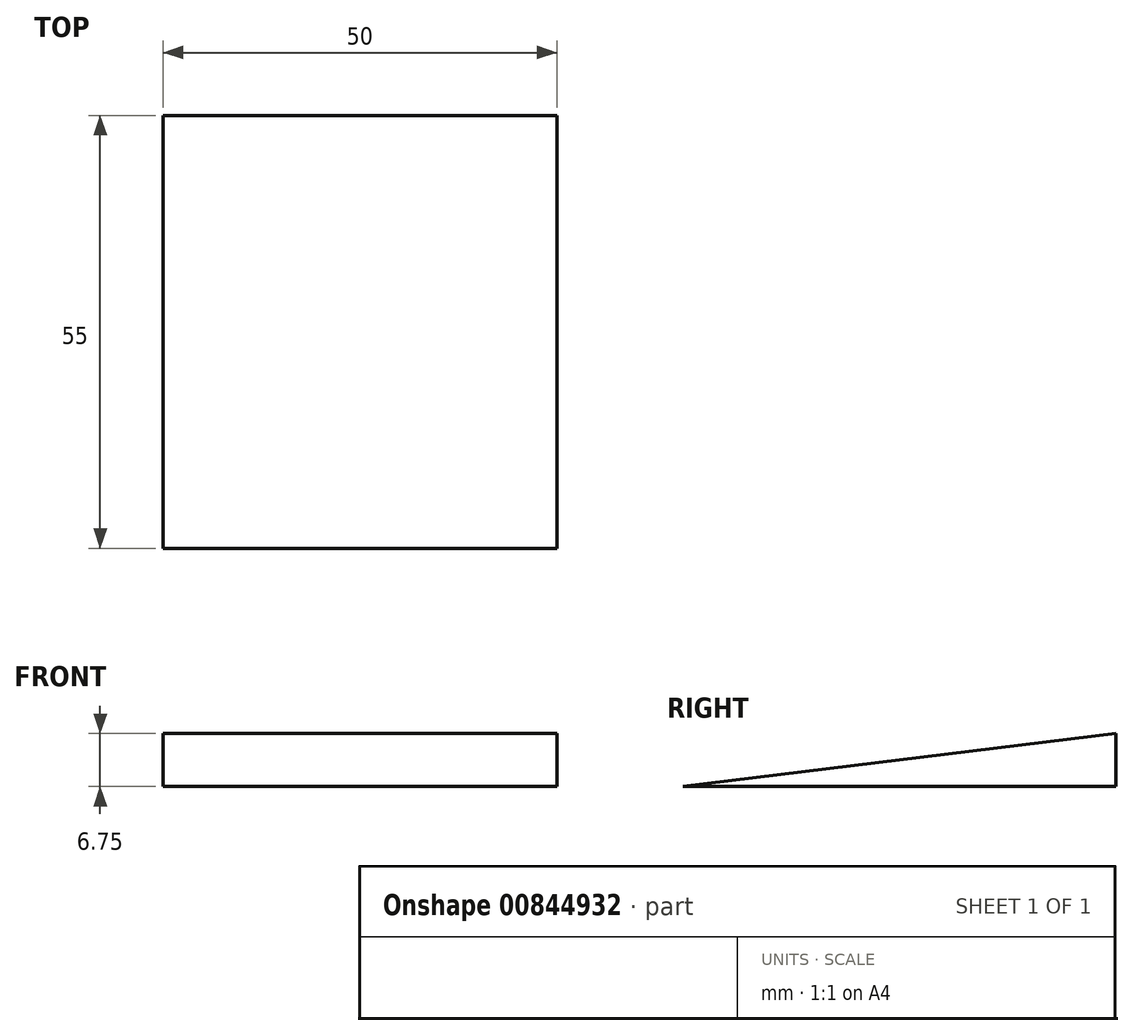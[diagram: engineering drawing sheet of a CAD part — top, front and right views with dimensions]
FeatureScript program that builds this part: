
annotation { "Feature Type Name" : "Feature", "Feature Type Description" : "" }
export const myFeature = defineFeature(function(context is Context, id is Id, definition is map)
    precondition{}
    {
        {
            var Q0;
            Q0=qCreatedBy(makeId("Top.planeOp"),FACE);
            var sketch = newSketch(context, id + "F0", { "sketchPlane" : qUnion([Q0])});
            skLineSegment(sketch, "E0.bottom", {"start": v(25, 27.5) * mm, "end": v(-25, 27.5) * mm});
            skLineSegment(sketch, "E0.top", {"start": v(25, -27.5) * mm, "end": v(-25, -27.5) * mm});
            skLineSegment(sketch, "E0.left", {"start": v(25, 27.5) * mm, "end": v(25, -27.5) * mm});
            skLineSegment(sketch, "E0.right", {"start": v(-25, 27.5) * mm, "end": v(-25, -27.5) * mm});
            skPoint(sketch, "E0.middle", {"position": v(0, 0) * mm});
            skSolve(sketch);
        }
        {
            var Q0;
            Q0=qCreatedBy(makeId("Top.planeOp"),FACE);
            var sketch = newSketch(context, id + "F1", { "sketchPlane" : qUnion([Q0])});
            skLineSegment(sketch, "E1", {"start": v(-25, -27.5) * mm, "end": v(25, -27.5) * mm});
            skSolve(sketch);
        }
        {
            var Q0;
            Q0 = qBodyType(qCreatedBy(id + "F1" ,EDGE), BodyType.WIRE);
            cPlane(context, id + "F2", {"entities" : qUnion([Q0]), "cplaneType" : CPlaneType.LINE_ANGLE, "offset" : 25 * mm, "angle" : 97 * degree, "width" : 150 * mm, "height" : 150 * mm});
        }
        {
            var Q0;
            Q0=makeQuery(id+"F0.imprint","IMPRINT",FACE,{"disambiguationData":[TD([[makeQuery(id+"F0.imprint","IMPRINT",EDGE,{"derivedFrom":sQuery(id+"F0.wireOp",EDGE,"E0.bottom")}),1.0]])]});
            var Q1;
            Q1=qCreatedBy(id+"F2.planeOp",FACE);
            var Q2;
            Q2=qCreatedBy(id+"F2.planeOp",FACE);
            extrude(context, id + "F3", {"entities" : qUnion([Q0]), "endBound" : BoundingType.UP_TO_SURFACE, "depth" : 25 * mm, "endBoundEntityFace" : qUnion([Q1]), "offsetDistance" : 25 * mm});
        }
    });
